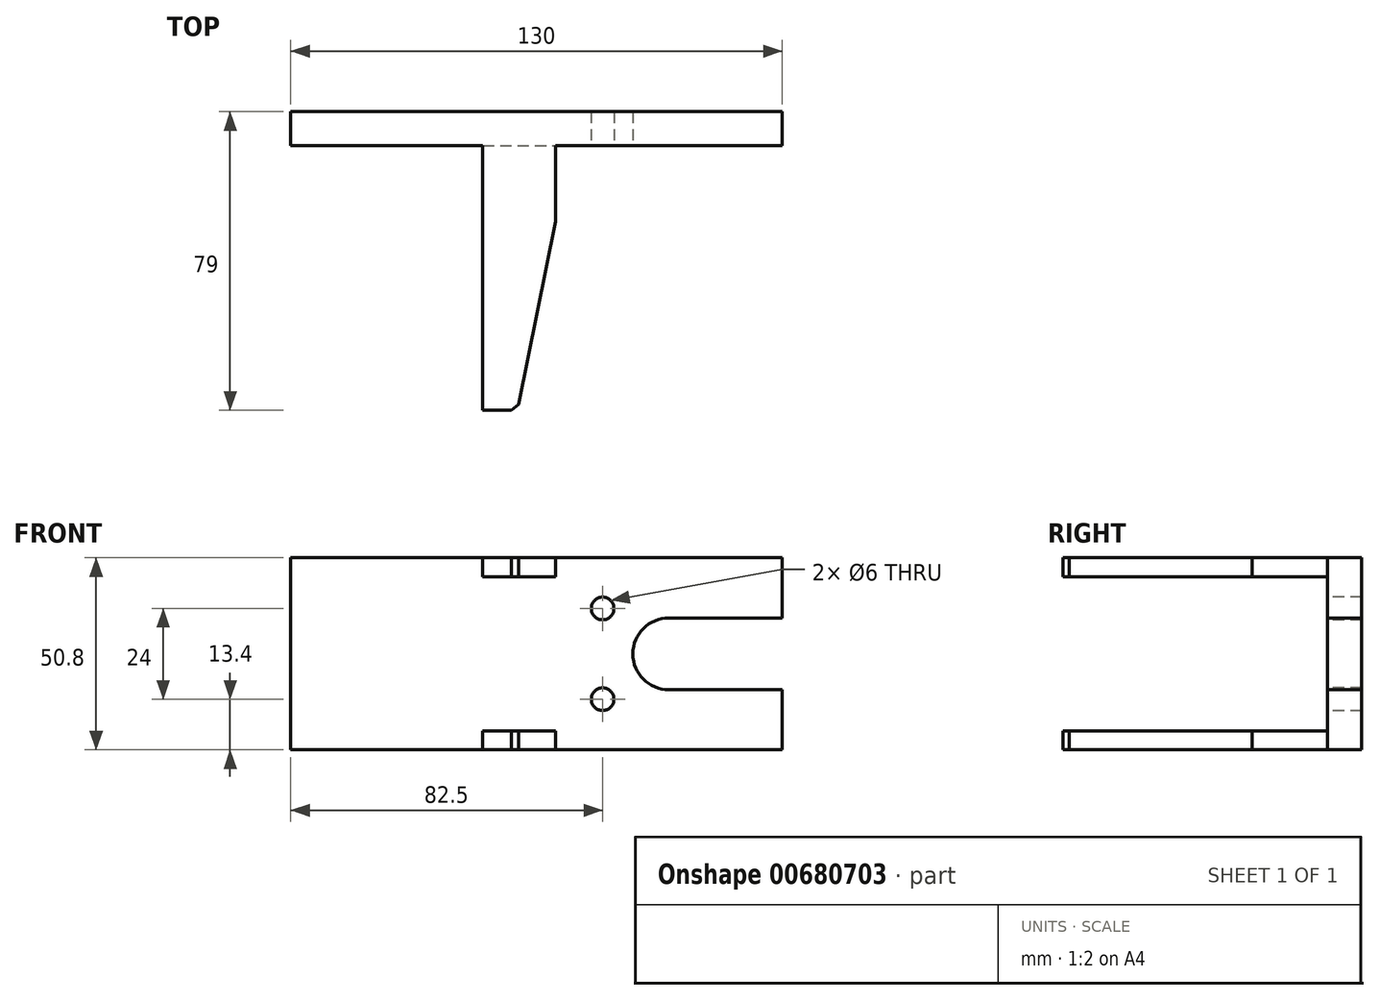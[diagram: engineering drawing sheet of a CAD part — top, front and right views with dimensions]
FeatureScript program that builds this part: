
annotation { "Feature Type Name" : "Feature", "Feature Type Description" : "" }
export const myFeature = defineFeature(function(context is Context, id is Id, definition is map)
    precondition{}
    {
        {
            var Q0;
            Q0=qCreatedBy(makeId("Front.planeOp"),FACE);
            var sketch = newSketch(context, id + "F0", { "sketchPlane" : qUnion([Q0])});
            skLineSegment(sketch, "E0.bottom", {"start": v(-70, 25.4) * mm, "end": v(60, 25.4) * mm});
            skLineSegment(sketch, "E0.top", {"start": v(-70, -25.4) * mm, "end": v(60, -25.4) * mm});
            skLineSegment(sketch, "E0.left", {"start": v(-70, 25.4) * mm, "end": v(-70, -25.4) * mm});
            skLineSegment(sketch, "E0.right", {"start": v(60, 25.4) * mm, "end": v(60, 9.5) * mm});
            skLineSegment(sketch, "E1", {"start": v(60, 9.5) * mm, "end": v(30, 9.5) * mm});
            skLineSegment(sketch, "E2", {"start": v(30, -9.5) * mm, "end": v(60, -9.5) * mm});
            skPoint(sketch, "E3.center.orphan", {"position": v(60, 0) * mm});
            skLineSegment(sketch, "E4.trimOffspring", {"start": v(60, -9.5) * mm, "end": v(60, -25.4) * mm});
            skPoint(sketch, "E5.startSnap0", {"position": v(30, 9.5) * mm});
            skPoint(sketch, "E6", {"position": v(30, 0) * mm});
            skArc(sketch, "E7", {"start": v(30, 9.5) * mm, "mid": v(20.5, 0) * mm, "end": v(30, -9.5) * mm});
            skCircle(sketch, "E8", {"center": v(12.5, -12) * mm, "radius": 3 * mm});
            skCircle(sketch, "E9.MirrorC", {"center": v(12.5, 12) * mm, "radius": 3 * mm});
            skLineSegment(sketch, "E10", {"start": v(-19.2, 20.4) * mm, "end": v(0.8, 20.4) * mm});
            skLineSegment(sketch, "E11", {"start": v(-19.2, 25.4) * mm, "end": v(-19.2, 20.4) * mm});
            skLineSegment(sketch, "E12.MirrorCS", {"start": v(-19.2, -20.4) * mm, "end": v(0.8, -20.4) * mm});
            skLineSegment(sketch, "E13.bottom", {"start": v(-19.2, 25.4) * mm, "end": v(0.8, 25.4) * mm});
            skLineSegment(sketch, "E13.right", {"start": v(0.8, 25.4) * mm, "end": v(0.8, 20.4) * mm});
            skLineSegment(sketch, "E14.MirrorCS", {"start": v(-19.2, -25.4) * mm, "end": v(-19.2, -20.4) * mm});
            skLineSegment(sketch, "E15.MirrorCS", {"start": v(0.8, -25.4) * mm, "end": v(0.8, -20.4) * mm});
            skLineSegment(sketch, "E16.MirrorCS", {"start": v(-19.2, -25.4) * mm, "end": v(0.8, -25.4) * mm});
            skSolve(sketch);
        }
        {
            var Q0;
            Q0 = qSketchRegion(id + "F0", true);
            extrude(context, id + "F1", {"entities" : qUnion([Q0]), "oppositeDirection" : true, "depth" : 9 * mm, "offsetDistance" : 25 * mm});
        }
        {
            var Q0;
            Q0=makeQuery(id+"F1.opExtrude","CAP_FACE",FACE,{"disambiguationData":[OSD([sQuery(id+"F0.wireOp",EDGE,"E0.bottom"),sQuery(id+"F0.wireOp",EDGE,"E0.top"),sQuery(id+"F0.wireOp",EDGE,"E0.left"),sQuery(id+"F0.wireOp",EDGE,"E0.right"),sQuery(id+"F0.wireOp",EDGE,"E1"),sQuery(id+"F0.wireOp",EDGE,"E2"),sQuery(id+"F0.wireOp",EDGE,"E4.trimOffspring"),sQuery(id+"F0.wireOp",EDGE,"E7"),sQuery(id+"F0.wireOp",EDGE,"E8"),sQuery(id+"F0.wireOp",EDGE,"E9.MirrorC"),sQuery(id+"F0.wireOp",EDGE,"E13.bottom"),sQuery(id+"F0.wireOp",EDGE,"E16.MirrorCS")])],"isStart":true});
            var sketch = newSketch(context, id + "F2", { "sketchPlane" : qUnion([Q0])});
            skLineSegment(sketch, "E17", {"start": v(-70, 25.4) * mm, "end": v(-19.2, 25.4) * mm, "construction": true});
            skLineSegment(sketch, "E18", {"start": v(-19.2, 25.4) * mm, "end": v(-19.2, -25.4) * mm, "construction": true});
            skLineSegment(sketch, "E19.bottom", {"start": v(-19.2, 25.4) * mm, "end": v(0, 25.4) * mm});
            skLineSegment(sketch, "E19.top", {"start": v(-19.2, 20.4) * mm, "end": v(0, 20.4) * mm});
            skLineSegment(sketch, "E19.left", {"start": v(-19.2, 25.4) * mm, "end": v(-19.2, 20.4) * mm});
            skLineSegment(sketch, "E19.right", {"start": v(0, 25.4) * mm, "end": v(0, 20.4) * mm});
            skLineSegment(sketch, "E20.MirrorCS", {"start": v(0, -25.4) * mm, "end": v(0, -20.4) * mm});
            skLineSegment(sketch, "E21.MirrorCS", {"start": v(-19.2, -25.4) * mm, "end": v(-19.2, -20.4) * mm});
            skLineSegment(sketch, "E22.MirrorCS", {"start": v(-19.2, -20.4) * mm, "end": v(0, -20.4) * mm});
            skLineSegment(sketch, "E23.MirrorCS", {"start": v(-19.2, -25.4) * mm, "end": v(0, -25.4) * mm});
            skSolve(sketch);
        }
        {
            var Q0;
            Q0=makeQuery(id+"F2.imprint","IMPRINT",FACE,{"disambiguationData":[TD([[makeQuery(id+"F2.imprint","IMPRINT",EDGE,{"derivedFrom":sQuery(id+"F2.wireOp",EDGE,"E19.bottom")}),-1.0]])]});
            var Q1;
            Q1=makeQuery(id+"F2.imprint","IMPRINT",FACE,{"disambiguationData":[TD([[makeQuery(id+"F2.imprint","IMPRINT",EDGE,{"derivedFrom":sQuery(id+"F2.wireOp",EDGE,"E20.MirrorCS")}),1.0]])]});
            extrude(context, id + "F3", {"entities" : qUnion([Q0, Q1]), "operationType" : NewBodyOperationType.ADD, "depth" : 70 * mm, "offsetDistance" : 25 * mm});
        }
        {
            var Q0;
            Q0=makeQuery(id+"F3.opExtrude","CAP_EDGE",EDGE,{"disambiguationData":[OSD([sQuery(id+"F2.wireOp",EDGE,"E19.right")])],"isStart":false});
            chamfer(context, id + "F4", {"entities" : qUnion([Q0]), "chamferType" : ChamferType.TWO_OFFSETS, "width1" : 10 * mm, "oppositeDirection" : true, "width2" : 50 * mm, "tangentPropagation" : true});
        }
        {
            var Q0;
            Q0=makeQuery(id+"F3.opExtrude","CAP_EDGE",EDGE,{"disambiguationData":[OSD([sQuery(id+"F2.wireOp",EDGE,"E20.MirrorCS")])],"isStart":false});
            chamfer(context, id + "F5", {"entities" : qUnion([Q0]), "chamferType" : ChamferType.TWO_OFFSETS, "width1" : 10 * mm, "oppositeDirection" : false, "width2" : 50 * mm, "tangentPropagation" : true});
        }
        {
            var Q0;
            {var subQ0=sQuery(id+"F2.wireOp",EDGE,"E19.right");Q0=makeQuery(id+"F4.opChamfer","BLEND_EDGE",EDGE,{"blendedFrom":[makeQuery(id+"F3.opExtrude","CAP_EDGE",EDGE,{"disambiguationData":[OSD([subQ0])],"isStart":false}),makeQuery(id+"F3.opExtrude","CAP_FACE",FACE,{"disambiguationData":[OSD([sQuery(id+"F2.wireOp",EDGE,"E19.bottom"),sQuery(id+"F2.wireOp",EDGE,"E19.top"),sQuery(id+"F2.wireOp",EDGE,"E19.left"),subQ0])],"isStart":false})],"blendedInto":[makeQuery(id+"F3.opExtrude","CAP_FACE",FACE,{"disambiguationData":[OSD([sQuery(id+"F2.wireOp",EDGE,"E19.bottom"),sQuery(id+"F2.wireOp",EDGE,"E19.top"),sQuery(id+"F2.wireOp",EDGE,"E19.left"),subQ0])],"isStart":false})]});}
            var Q1;
            {var subQ0=sQuery(id+"F2.wireOp",EDGE,"E20.MirrorCS");Q1=makeQuery(id+"F5.opChamfer","BLEND_EDGE",EDGE,{"blendedFrom":[makeQuery(id+"F3.opExtrude","CAP_EDGE",EDGE,{"disambiguationData":[OSD([subQ0])],"isStart":false}),makeQuery(id+"F3.opExtrude","CAP_FACE",FACE,{"disambiguationData":[OSD([subQ0,sQuery(id+"F2.wireOp",EDGE,"E21.MirrorCS"),sQuery(id+"F2.wireOp",EDGE,"E22.MirrorCS"),sQuery(id+"F2.wireOp",EDGE,"E23.MirrorCS")])],"isStart":false})],"blendedInto":[makeQuery(id+"F3.opExtrude","CAP_FACE",FACE,{"disambiguationData":[OSD([subQ0,sQuery(id+"F2.wireOp",EDGE,"E21.MirrorCS"),sQuery(id+"F2.wireOp",EDGE,"E22.MirrorCS"),sQuery(id+"F2.wireOp",EDGE,"E23.MirrorCS")])],"isStart":false})]});}
            chamfer(context, id + "F6", {"entities" : qUnion([Q0, Q1]), "width" : 2 * mm, "tangentPropagation" : true});
        }
    });
